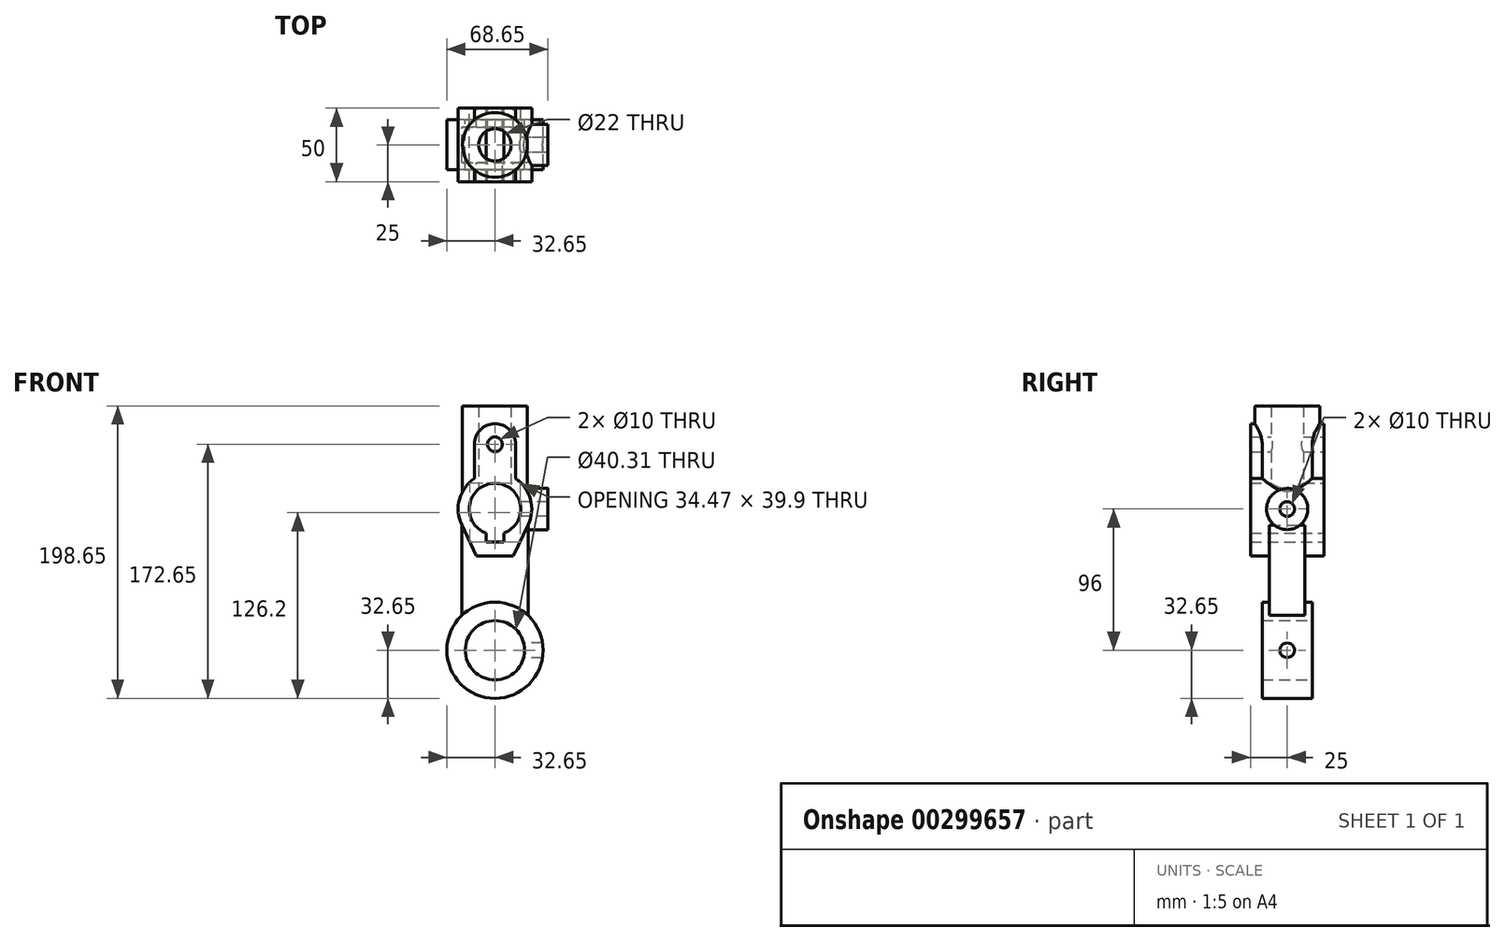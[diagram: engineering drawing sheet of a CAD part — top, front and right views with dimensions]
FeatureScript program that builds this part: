
annotation { "Feature Type Name" : "Feature", "Feature Type Description" : "" }
export const myFeature = defineFeature(function(context is Context, id is Id, definition is map)
    precondition{}
    {
        {
            var Q0;
            Q0=qCreatedBy(makeId("Front.planeOp"),FACE);
            var sketch = newSketch(context, id + "F0", { "sketchPlane" : qUnion([Q0])});
            skCircle(sketch, "E0", {"center": v(0, 0) * mm, "radius": 20.15 * mm});
            skCircle(sketch, "E1", {"center": v(0, 0) * mm, "radius": 32.65 * mm});
            skSolve(sketch);
        }
        {
            var Q0;
            Q0=makeQuery(id+"F0.imprint","IMPRINT",FACE,{"disambiguationData":[TD([[makeQuery(id+"F0.imprint","IMPRINT",EDGE,{"derivedFrom":sQuery(id+"F0.wireOp",EDGE,"E0")}),-1.0]])]});
            var Q1;
            Q1=sQuery(id+"F0.wireOp",EDGE,"E1");
            extrude(context, id + "F1", {"entities" : qUnion([Q0]), "surfaceEntities" : qUnion([Q1]), "depth" : 17 * mm, "hasSecondDirection" : true, "secondDirectionOppositeDirection" : true, "secondDirectionDepth" : 17 * mm});
        }
        {
            var Q0;
            Q0=qCreatedBy(makeId("Front.planeOp"),FACE);
            var sketch = newSketch(context, id + "F2", { "sketchPlane" : qUnion([Q0])});
            skArc(sketch, "E2", {"start": v(6, 79.56) * mm, "mid": v(0, 113.5) * mm, "end": v(-6, 79.56) * mm});
            skArc(sketch, "E3", {"start": v(-14, 116.71) * mm, "mid": v(-24.11, 102.6) * mm, "end": v(-22.6, 85.3) * mm});
            skCircle(sketch, "E4", {"center": v(0, 140) * mm, "radius": 5 * mm});
            skArc(sketch, "E5", {"start": v(-14, 140) * mm, "mid": v(0, 154) * mm, "end": v(14, 140) * mm});
            skLineSegment(sketch, "E6", {"start": v(-14, 140) * mm, "end": v(-14, 116.71) * mm});
            skLineSegment(sketch, "E7", {"start": v(14, 140) * mm, "end": v(14, 116.71) * mm});
            skLineSegment(sketch, "E8", {"start": v(-6, 73.6) * mm, "end": v(6, 73.6) * mm});
            skLineSegment(sketch, "E9", {"start": v(-12.5, 64) * mm, "end": v(12.5, 64) * mm});
            skLineSegment(sketch, "E10", {"start": v(-6, 73.6) * mm, "end": v(-6, 79.56) * mm});
            skLineSegment(sketch, "E11", {"start": v(6, 73.6) * mm, "end": v(6, 79.56) * mm});
            skLineSegment(sketch, "E12", {"start": v(12.5, 64) * mm, "end": v(22.6, 85.3) * mm});
            skLineSegment(sketch, "E13", {"start": v(-12.5, 64) * mm, "end": v(-22.6, 85.3) * mm});
            skArc(sketch, "E14.trimOffspring", {"start": v(22.6, 85.3) * mm, "mid": v(24.11, 102.6) * mm, "end": v(14, 116.71) * mm});
            skSolve(sketch);
        }
        {
            var Q0;
            Q0 = qSketchRegion(id + "F2", true);
            extrude(context, id + "F3", {"entities" : qUnion([Q0]), "depth" : 25 * mm, "hasSecondDirection" : true, "secondDirectionOppositeDirection" : true, "secondDirectionDepth" : 25 * mm});
        }
        {
            var Q0;
            Q0=qCreatedBy(makeId("Front.planeOp"),FACE);
            var sketch = newSketch(context, id + "F4", { "sketchPlane" : qUnion([Q0])});
            skLineSegment(sketch, "E15.top", {"start": v(-22.5, 21.23) * mm, "end": v(22.5, 21.23) * mm});
            skLineSegment(sketch, "E15.left", {"start": v(-22.5, 85.1) * mm, "end": v(-22.5, 21.23) * mm});
            skLineSegment(sketch, "E15.right", {"start": v(22.5, 85.1) * mm, "end": v(22.5, 21.23) * mm});
            skLineSegment(sketch, "E16.0.0", {"start": v(12.5, 64) * mm, "end": v(22.6, 85.3) * mm});
            skLineSegment(sketch, "E16.0.6", {"start": v(-22.6, 85.3) * mm, "end": v(-12.5, 64) * mm});
            skLineSegment(sketch, "E16.0.7", {"start": v(-12.5, 64) * mm, "end": v(12.5, 64) * mm});
            skPoint(sketch, "E16.0.2.start.orphan", {"position": v(14, 116.71) * mm});
            skPoint(sketch, "E16.0.3.start.orphan", {"position": v(14, 140) * mm});
            skPoint(sketch, "E16.0.4.end.orphan", {"position": v(-14, 116.71) * mm});
            skPoint(sketch, "E16.0.4.start.orphan", {"position": v(-14, 140) * mm});
            skSolve(sketch);
        }
        {
            var Q0;
            Q0 = qSketchRegion(id + "F4", true);
            extrude(context, id + "F5", {"entities" : qUnion([Q0]), "operationType" : NewBodyOperationType.ADD, "depth" : 12 * mm, "hasSecondDirection" : true, "secondDirectionOppositeDirection" : true, "secondDirectionDepth" : 12 * mm});
        }
        {
            var Q0;
            Q0=qCreatedBy(makeId("Right.planeOp"),FACE);
            var sketch = newSketch(context, id + "F6", { "sketchPlane" : qUnion([Q0])});
            skCircle(sketch, "E17", {"center": v(0, 0) * mm, "radius": 5 * mm});
            skSolve(sketch);
        }
        {
            var Q0;
            Q0 = qSketchRegion(id + "F6", true);
            extrude(context, id + "F7", {"entities" : qUnion([Q0]), "operationType" : NewBodyOperationType.REMOVE, "endBound" : BoundingType.THROUGH_ALL, "depth" : 25 * mm});
        }
        {
            var Q0;
            Q0=qCreatedBy(makeId("Front.planeOp"),FACE);
            var sketch = newSketch(context, id + "F8", { "sketchPlane" : qUnion([Q0])});
            skLineSegment(sketch, "E18.bottom", {"start": v(11, 166) * mm, "end": v(22, 166) * mm});
            skLineSegment(sketch, "E18.top", {"start": v(11, 90.94) * mm, "end": v(22, 90.94) * mm});
            skLineSegment(sketch, "E18.left", {"start": v(11, 166) * mm, "end": v(11, 90.94) * mm});
            skLineSegment(sketch, "E18.right", {"start": v(22, 166) * mm, "end": v(22, 90.94) * mm});
            skLineSegment(sketch, "E19", {"start": v(0, 0) * mm, "end": v(0, 166) * mm, "construction": true});
            skSolve(sketch);
        }
        {
            var Q0;
            Q0 = qSketchRegion(id + "F8", true);
            var Q1;
            Q1=sQuery(id+"F8.wireOp",EDGE,"E19");
            revolve(context, id + "F9", {"operationType" : NewBodyOperationType.ADD, "entities" : qUnion([Q0]), "axis" : qUnion([Q1]), "revolveType" : RevolveType.FULL});
        }
        {
            var Q0;
            Q0=qCreatedBy(makeId("Right.planeOp"),FACE);
            var sketch = newSketch(context, id + "F10", { "sketchPlane" : qUnion([Q0])});
            skCircle(sketch, "E20", {"center": v(0, 96) * mm, "radius": 14 * mm});
            skCircle(sketch, "E21", {"center": v(0, 96) * mm, "radius": 5 * mm});
            skSolve(sketch);
        }
        {
            var Q0;
            Q0 = qSketchRegion(id + "F10", true);
            extrude(context, id + "F11", {"entities" : qUnion([Q0]), "operationType" : NewBodyOperationType.ADD, "depth" : 36 * mm});
        }
        {
            var Q0;
            Q0=makeQuery(id+"F9.opRevolve","SWEPT_FACE",FACE,{"disambiguationData":[OSD([sQuery(id+"F8.wireOp",EDGE,"E18.bottom")])]});
            var sketch = newSketch(context, id + "F12", { "sketchPlane" : qUnion([Q0])});
            skCircle(sketch, "E22.0", {"center": v(0, 0) * mm, "radius": 11 * mm});
            skSolve(sketch);
        }
        {
            var Q0;
            Q0=makeQuery(id+"F12.imprint","IMPRINT",FACE,{"disambiguationData":[TD([[makeQuery(id+"F12.imprint","IMPRINT",EDGE,{"derivedFrom":sQuery(id+"F12.wireOp",EDGE,"E22.0")}),-1.0]])]});
            var Q1;
            Q1=sQuery(id+"F12.wireOp",EDGE,"E22.0");
            extrude(context, id + "F13", {"entities" : qUnion([Q0]), "operationType" : NewBodyOperationType.REMOVE, "surfaceEntities" : qUnion([Q1]), "oppositeDirection" : true, "depth" : (166 - 96) * mm});
        }
        {
            var Q0;
            Q0=makeQuery(id+"F11.opExtrude","CAP_FACE",FACE,{"disambiguationData":[OSD([sQuery(id+"F10.wireOp",EDGE,"E20"),sQuery(id+"F10.wireOp",EDGE,"E21")])],"isStart":false});
            var sketch = newSketch(context, id + "F14", { "sketchPlane" : qUnion([Q0])});
            skCircle(sketch, "E23.0", {"center": v(0, 96) * mm, "radius": 5 * mm});
            skSolve(sketch);
        }
        {
            var Q0;
            Q0=makeQuery(id+"F14.imprint","IMPRINT",FACE,{"disambiguationData":[TD([[makeQuery(id+"F14.imprint","IMPRINT",EDGE,{"derivedFrom":sQuery(id+"F14.wireOp",EDGE,"E23.0")}),1.0]])]});
            var Q1;
            Q1=sQuery(id+"F14.wireOp",EDGE,"E23.0");
            extrude(context, id + "F15", {"entities" : qUnion([Q0]), "operationType" : NewBodyOperationType.REMOVE, "surfaceEntities" : qUnion([Q1]), "oppositeDirection" : true, "depth" : 36 * mm});
        }
        {
            var Q0;
            Q0=makeQuery(id+"F3.opExtrude","CAP_FACE",FACE,{"disambiguationData":[OSD([sQuery(id+"F2.wireOp",EDGE,"E2"),sQuery(id+"F2.wireOp",EDGE,"E3"),sQuery(id+"F2.wireOp",EDGE,"E4"),sQuery(id+"F2.wireOp",EDGE,"E5"),sQuery(id+"F2.wireOp",EDGE,"E6"),sQuery(id+"F2.wireOp",EDGE,"E7"),sQuery(id+"F2.wireOp",EDGE,"E8"),sQuery(id+"F2.wireOp",EDGE,"E9"),sQuery(id+"F2.wireOp",EDGE,"E10"),sQuery(id+"F2.wireOp",EDGE,"E11"),sQuery(id+"F2.wireOp",EDGE,"E12"),sQuery(id+"F2.wireOp",EDGE,"E13"),sQuery(id+"F2.wireOp",EDGE,"E14.trimOffspring")])],"isStart":false});
            var sketch = newSketch(context, id + "F16", { "sketchPlane" : qUnion([Q0])});
            skCircle(sketch, "E24.0", {"center": v(0, 140) * mm, "radius": 5 * mm});
            skArc(sketch, "E25.0", {"start": v(6, 79.56) * mm, "mid": v(0, 113.5) * mm, "end": v(-6, 79.56) * mm});
            skLineSegment(sketch, "E26.0", {"start": v(-6, 73.6) * mm, "end": v(6, 73.6) * mm});
            skLineSegment(sketch, "E27", {"start": v(-6, 79.56) * mm, "end": v(-6, 73.6) * mm});
            skLineSegment(sketch, "E28", {"start": v(6, 73.6) * mm, "end": v(6, 79.56) * mm});
            skSolve(sketch);
        }
        {
            var Q0;
            Q0 = qSketchRegion(id + "F16", true);
            extrude(context, id + "F17", {"entities" : qUnion([Q0]), "operationType" : NewBodyOperationType.REMOVE, "oppositeDirection" : true, "depth" : 50 * mm});
        }
    });
